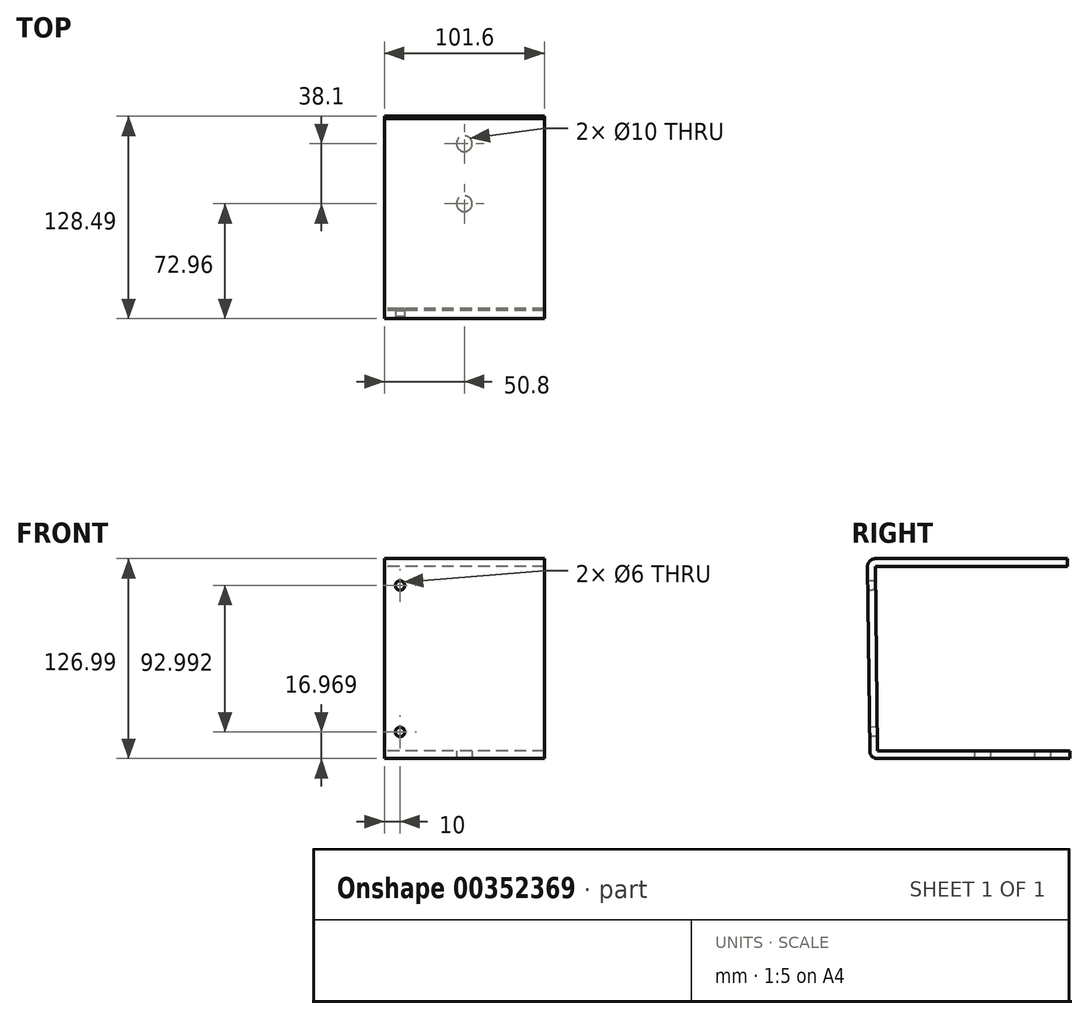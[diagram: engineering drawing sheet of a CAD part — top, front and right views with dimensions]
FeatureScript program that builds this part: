
annotation { "Feature Type Name" : "Feature", "Feature Type Description" : "" }
export const myFeature = defineFeature(function(context is Context, id is Id, definition is map)
    precondition{}
    {
        {
            var Q0;
            Q0=qCreatedBy(makeId("Right.planeOp"),FACE);
            var sketch = newSketch(context, id + "F0", { "sketchPlane" : qUnion([Q0])});
            skLineSegment(sketch, "E0", {"start": v(69.98, 55.95) * mm, "end": v(-51.96, 55.95) * mm});
            skLineSegment(sketch, "E1", {"start": v(-56.96, 50.9) * mm, "end": v(-55.53, -66.1) * mm});
            skLineSegment(sketch, "E2", {"start": v(-50.54, -71.04) * mm, "end": v(71.53, -71.04) * mm});
            skLineSegment(sketch, "E3.0", {"start": v(-50.54, -66.04) * mm, "end": v(71.53, -66.04) * mm});
            skLineSegment(sketch, "E3.1", {"start": v(-51.96, 50.95) * mm, "end": v(-50.54, -66.04) * mm});
            skLineSegment(sketch, "E3.2", {"start": v(69.98, 50.95) * mm, "end": v(-51.96, 50.95) * mm});
            skLineSegment(sketch, "E4", {"start": v(69.98, 55.95) * mm, "end": v(69.98, 50.95) * mm});
            skLineSegment(sketch, "E5", {"start": v(71.53, -66.04) * mm, "end": v(71.53, -71.04) * mm});
            skPoint(sketch, "E6.visualSharp", {"position": v(-57.02, 55.95) * mm});
            skArc(sketch, "E6.filletArc", {"start": v(-51.96, 55.95) * mm, "mid": v(-55.52, 54.47) * mm, "end": v(-56.96, 50.9) * mm});
            skPoint(sketch, "E7.visualSharp", {"position": v(-55.47, -71.04) * mm});
            skArc(sketch, "E7.filletArc", {"start": v(-55.53, -66.1) * mm, "mid": v(-54.05, -69.6) * mm, "end": v(-50.54, -71.04) * mm});
            skSolve(sketch);
        }
        {
            var Q0;
            Q0 = qSketchRegion(id + "F0", true);
            extrude(context, id + "F1", {"entities" : qUnion([Q0]), "endBound" : BoundingType.SYMMETRIC, "depth" : 101.6 * mm});
        }
        {
            var Q0;
            Q0=makeQuery(id+"F1.opExtrude","SWEPT_FACE",FACE,{"disambiguationData":[OSD([sQuery(id+"F0.wireOp",EDGE,"E2")])]});
            var sketch = newSketch(context, id + "F2", { "sketchPlane" : qUnion([Q0])});
            skCircle(sketch, "E8", {"center": v(0, -16) * mm, "radius": 5 * mm});
            skCircle(sketch, "E9", {"center": v(0, -54.1) * mm, "radius": 5 * mm});
            skSolve(sketch);
        }
        {
            var Q0;
            Q0 = qSketchRegion(id + "F2", true);
            extrude(context, id + "F3", {"entities" : qUnion([Q0]), "operationType" : NewBodyOperationType.REMOVE, "endBound" : BoundingType.UP_TO_NEXT, "oppositeDirection" : true, "depth" : 25 * mm});
        }
        {
            var Q0;
            Q0=makeQuery(id+"F1.opExtrude","SWEPT_FACE",FACE,{"disambiguationData":[OSD([sQuery(id+"F0.wireOp",EDGE,"E1")])]});
            var sketch = newSketch(context, id + "F4", { "sketchPlane" : qUnion([Q0])});
            skCircle(sketch, "E10", {"center": v(-40.8, 39.58) * mm, "radius": 3 * mm});
            skCircle(sketch, "E11", {"center": v(-40.8, -53.42) * mm, "radius": 3 * mm});
            skSolve(sketch);
        }
        {
            var Q0;
            Q0 = qSketchRegion(id + "F4", true);
            extrude(context, id + "F5", {"entities" : qUnion([Q0]), "operationType" : NewBodyOperationType.REMOVE, "endBound" : BoundingType.THROUGH_ALL, "oppositeDirection" : true, "depth" : 25 * mm});
        }
    });
